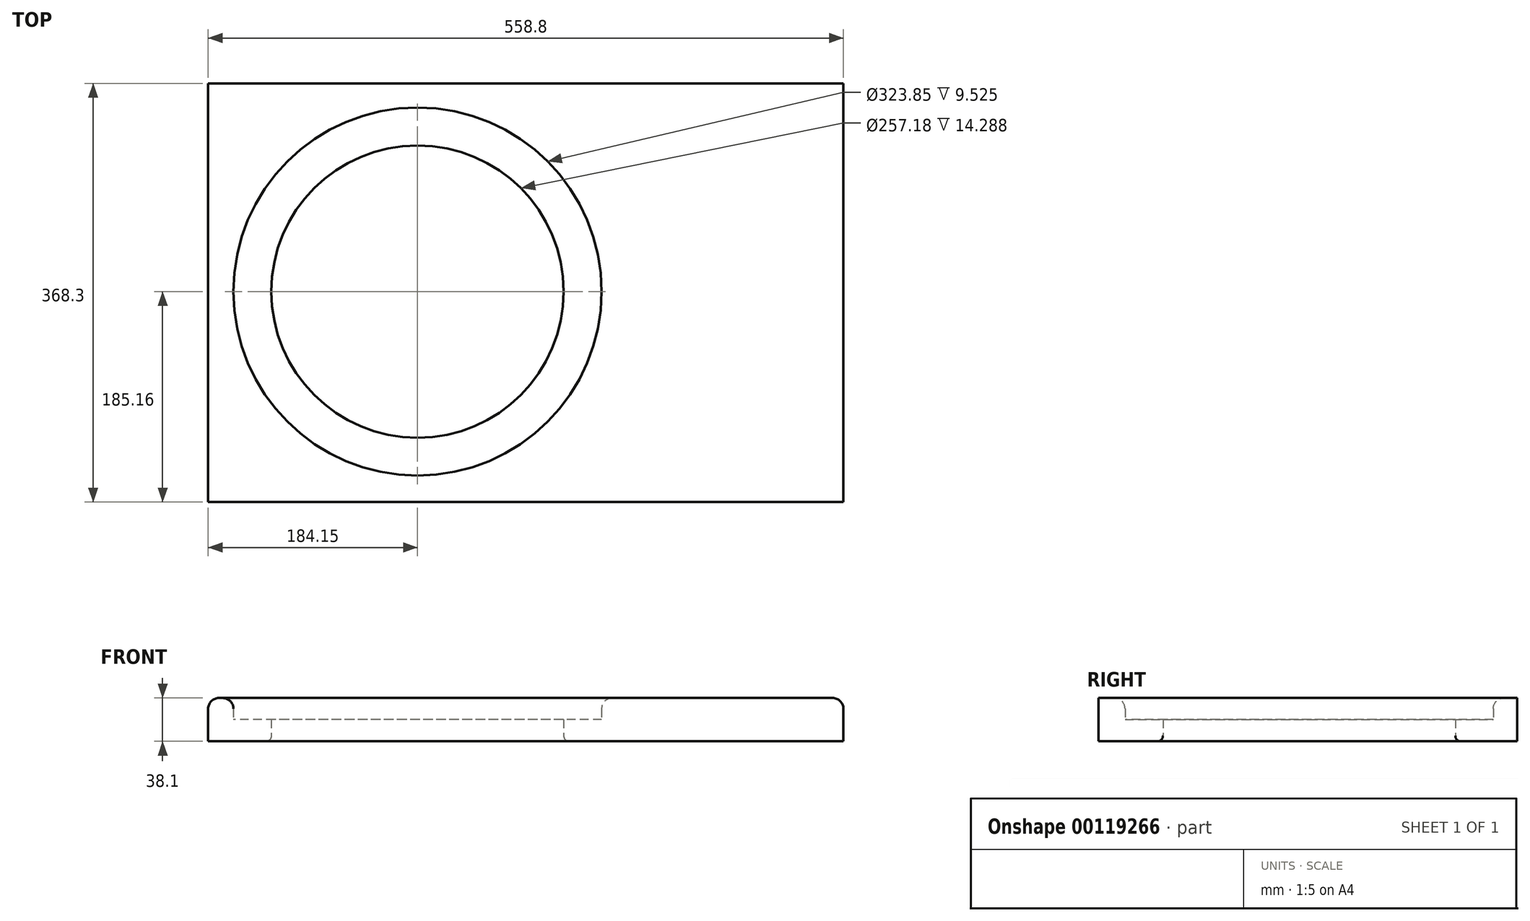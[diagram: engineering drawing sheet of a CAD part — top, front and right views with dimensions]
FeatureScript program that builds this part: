
annotation { "Feature Type Name" : "Feature", "Feature Type Description" : "" }
export const myFeature = defineFeature(function(context is Context, id is Id, definition is map)
    precondition{}
    {
        {
            var Q0;
            Q0=qCreatedBy(makeId("Top.planeOp"),FACE);
            var sketch = newSketch(context, id + "F0", { "sketchPlane" : qUnion([Q0])});
            skLineSegment(sketch, "E0.bottom", {"start": v(0, 0) * mm, "end": v(558.8, 0) * mm});
            skLineSegment(sketch, "E0.top", {"start": v(0, 368.3) * mm, "end": v(558.8, 368.3) * mm});
            skLineSegment(sketch, "E0.left", {"start": v(0, 0) * mm, "end": v(0, 368.3) * mm});
            skLineSegment(sketch, "E0.right", {"start": v(558.8, 0) * mm, "end": v(558.8, 368.3) * mm});
            skCircle(sketch, "E1", {"center": v(184.15, 185.16) * mm, "radius": 128.59 * mm});
            skCircle(sketch, "E2", {"center": v(184.15, 185.16) * mm, "radius": 161.93 * mm});
            skSolve(sketch);
        }
        {
            var Q0;
            Q0=makeQuery(id+"F0.imprint","IMPRINT",FACE,{"disambiguationData":[TD([[makeQuery(id+"F0.imprint","IMPRINT",EDGE,{"derivedFrom":sQuery(id+"F0.wireOp",EDGE,"E0.bottom")}),1.0]])]});
            extrude(context, id + "F1", {"entities" : qUnion([Q0]), "depth" : 38.1 * mm});
        }
        {
            var Q0;
            Q0=makeQuery(id+"F0.imprint","IMPRINT",FACE,{"disambiguationData":[TD([[makeQuery(id+"F0.imprint","IMPRINT",EDGE,{"derivedFrom":sQuery(id+"F0.wireOp",EDGE,"E1")}),-1.0]])]});
            extrude(context, id + "F2", {"entities" : qUnion([Q0]), "operationType" : NewBodyOperationType.ADD, "depth" : 19.05 * mm});
        }
        {
            var Q0;
            Q0=makeQuery(id+"F1.opExtrude","CAP_EDGE",EDGE,{"disambiguationData":[OSD([sQuery(id+"F0.wireOp",EDGE,"E2")])],"isStart":false});
            fillet(context, id + "F3", {"entities" : qUnion([Q0]), "radius" : 9.52 * mm, "tangentPropagation" : true, "allowEdgeOverflow" : false});
        }
        {
            var Q0;
            Q0=makeQuery(id+"F2.opExtrude","CAP_EDGE",EDGE,{"disambiguationData":[OSD([sQuery(id+"F0.wireOp",EDGE,"E1")])],"isStart":true});
            fillet(context, id + "F4", {"entities" : qUnion([Q0]), "radius" : 4.76 * mm, "tangentPropagation" : true, "allowEdgeOverflow" : false});
        }
        {
            var Q0;
            Q0=makeQuery(id+"F1.opExtrude","CAP_EDGE",EDGE,{"disambiguationData":[OSD([sQuery(id+"F0.wireOp",EDGE,"E0.right")])],"isStart":false});
            var Q1;
            Q1=makeQuery(id+"F1.opExtrude","CAP_EDGE",EDGE,{"disambiguationData":[OSD([sQuery(id+"F0.wireOp",EDGE,"E0.left")])],"isStart":false});
            fillet(context, id + "F5", {"entities" : qUnion([Q0, Q1]), "radius" : 9.52 * mm, "tangentPropagation" : true, "allowEdgeOverflow" : false});
        }
    });
